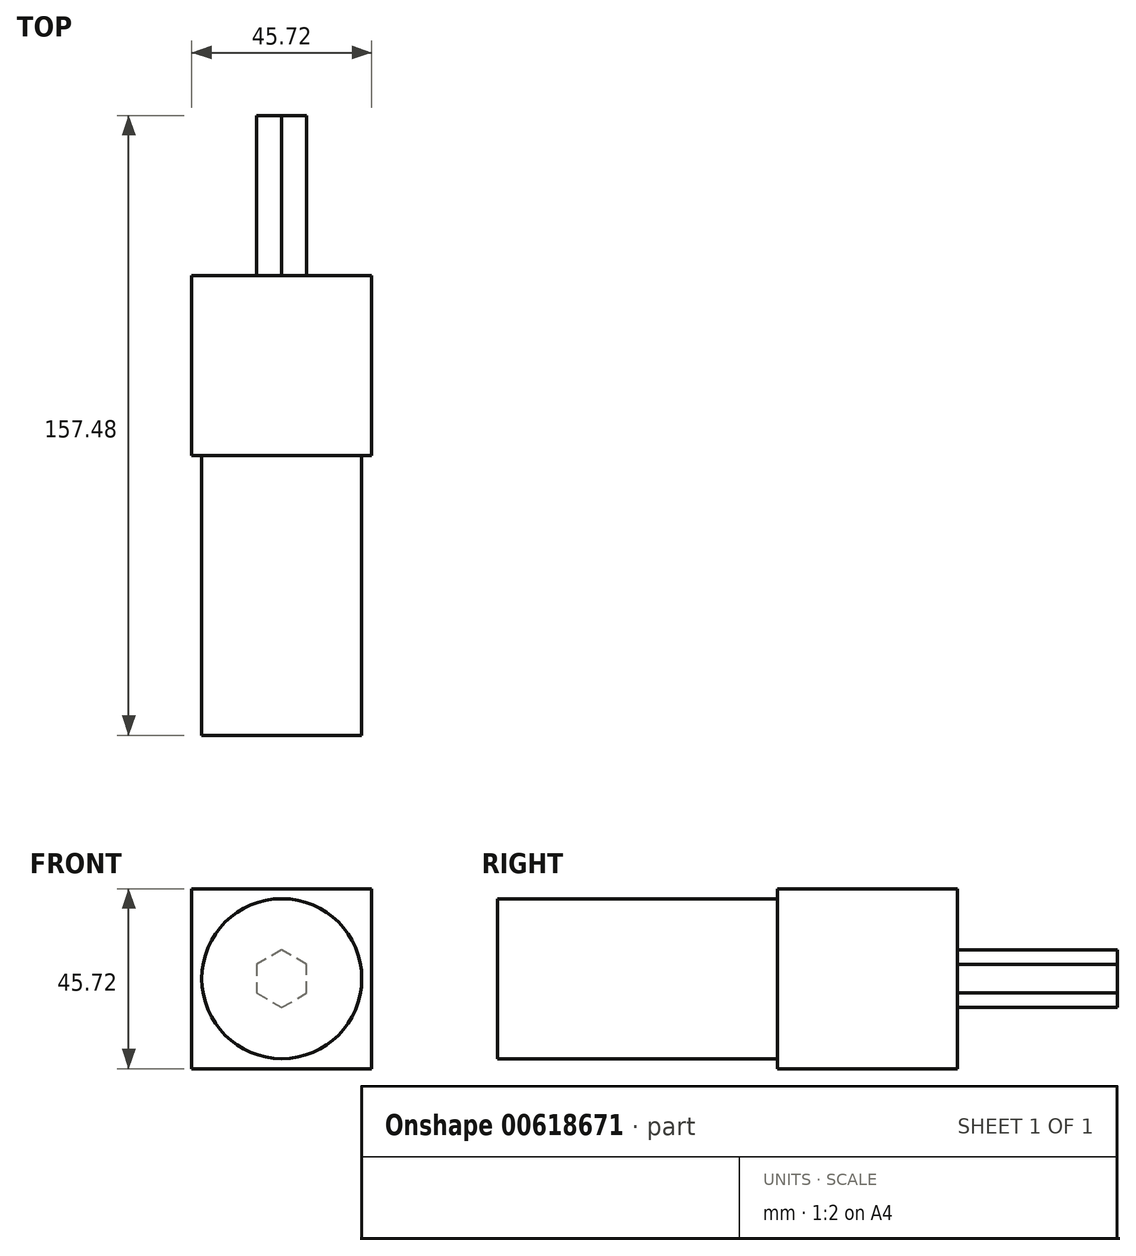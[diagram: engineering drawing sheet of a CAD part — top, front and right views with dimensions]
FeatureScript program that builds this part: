
annotation { "Feature Type Name" : "Feature", "Feature Type Description" : "" }
export const myFeature = defineFeature(function(context is Context, id is Id, definition is map)
    precondition{}
    {
        {
            var Q0;
            Q0=qCreatedBy(makeId("Front.planeOp"),FACE);
            var sketch = newSketch(context, id + "F0", { "sketchPlane" : qUnion([Q0])});
            skLineSegment(sketch, "E0.bottom", {"start": v(0, 0) * mm, "end": v(45.72, 0) * mm});
            skLineSegment(sketch, "E0.top", {"start": v(0, 45.72) * mm, "end": v(45.72, 45.72) * mm});
            skLineSegment(sketch, "E0.left", {"start": v(0, 0) * mm, "end": v(0, 45.72) * mm});
            skLineSegment(sketch, "E0.right", {"start": v(45.72, 0) * mm, "end": v(45.72, 45.72) * mm});
            skCircle(sketch, "E1", {"center": v(22.86, 22.86) * mm, "radius": 20.32 * mm});
            skPoint(sketch, "E1.centerSnap0", {"position": v(45.72, 22.86) * mm});
            skPoint(sketch, "E1.centerSnap1", {"position": v(22.86, 45.72) * mm});
            skSolve(sketch);
        }
        {
            var Q0;
            Q0=makeQuery(id+"F0.imprint","IMPRINT",FACE,{"disambiguationData":[TD([[makeQuery(id+"F0.imprint","IMPRINT",EDGE,{"derivedFrom":sQuery(id+"F0.wireOp",EDGE,"E0.bottom")}),1.0]])]});
            var Q1;
            Q1=makeQuery(id+"F0.imprint","IMPRINT",FACE,{"disambiguationData":[TD([[makeQuery(id+"F0.imprint","IMPRINT",EDGE,{"derivedFrom":sQuery(id+"F0.wireOp",EDGE,"E1")}),1.0]])]});
            extrude(context, id + "F1", {"entities" : qUnion([Q0, Q1]), "oppositeDirection" : true, "depth" : 45.72 * mm, "offsetDistance" : 25.4 * mm});
        }
        {
            var Q0;
            Q0=makeQuery(id+"F0.imprint","IMPRINT",FACE,{"disambiguationData":[TD([[makeQuery(id+"F0.imprint","IMPRINT",EDGE,{"derivedFrom":sQuery(id+"F0.wireOp",EDGE,"E1")}),1.0]])]});
            extrude(context, id + "F2", {"entities" : qUnion([Q0]), "operationType" : NewBodyOperationType.ADD, "depth" : 71.12 * mm, "offsetDistance" : 25.4 * mm});
        }
        {
            var Q0;
            Q0=makeQuery(id+"F1.opExtrude","CAP_FACE",FACE,{"disambiguationData":[OSD([sQuery(id+"F0.wireOp",EDGE,"E0.bottom"),sQuery(id+"F0.wireOp",EDGE,"E0.top"),sQuery(id+"F0.wireOp",EDGE,"E0.left"),sQuery(id+"F0.wireOp",EDGE,"E0.right")])],"isStart":false});
            var sketch = newSketch(context, id + "F3", { "sketchPlane" : qUnion([Q0])});
            skCircle(sketch, "E2.cCircle", {"center": v(-22.86, 22.86) * mm, "radius": 6.35 * mm, "construction": true});
            skPoint(sketch, "E2.cCircle.centerSnap0", {"position": v(0, 22.86) * mm});
            skPoint(sketch, "E2.cCircle.centerSnap1", {"position": v(-22.86, 45.72) * mm});
            skLineSegment(sketch, "E2.0", {"start": v(-16.51, 26.53) * mm, "end": v(-16.51, 19.2) * mm});
            skLineSegment(sketch, "E2.1", {"start": v(-16.5, 19.2) * mm, "end": v(-22.86, 15.53) * mm});
            skLineSegment(sketch, "E2.2", {"start": v(-22.86, 15.53) * mm, "end": v(-29.21, 19.2) * mm});
            skLineSegment(sketch, "E2.3", {"start": v(-29.21, 19.2) * mm, "end": v(-29.21, 26.53) * mm});
            skLineSegment(sketch, "E2.4", {"start": v(-29.21, 26.53) * mm, "end": v(-22.86, 30.2) * mm});
            skLineSegment(sketch, "E2.5", {"start": v(-22.86, 30.2) * mm, "end": v(-16.5, 26.53) * mm});
            skPoint(sketch, "E2.0.midPoint", {"position": v(-16.51, 22.86) * mm});
            skSolve(sketch);
        }
        {
            var Q0;
            Q0=makeQuery(id+"F3.imprint","IMPRINT",FACE,{"disambiguationData":[TD([[makeQuery(id+"F3.imprint","IMPRINT",EDGE,{"derivedFrom":sQuery(id+"F3.wireOp",EDGE,"E2.0")}),-1.0]])]});
            extrude(context, id + "F4", {"entities" : qUnion([Q0]), "operationType" : NewBodyOperationType.ADD, "depth" : 40.64 * mm, "offsetDistance" : 25.4 * mm});
        }
    });
